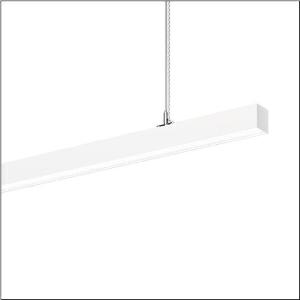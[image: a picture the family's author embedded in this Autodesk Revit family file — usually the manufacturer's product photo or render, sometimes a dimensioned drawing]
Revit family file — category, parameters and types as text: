
# Revit family: silica_r__21_51mx30tct9w_581c
name_source: partatom
category: Lighting Fixtures
units: mm (PartAtom-declared; Revit-internal decimal feet)

## family parameters
Cut with Voids When Loaded = No
Host = Face
Light Source = No
Part Type = Normal
Room Calculation Point = No
Round Connector Dimension = Use Diameter
Shared = No

## types (1)
- --- (1 x LED, 10300 lm, 84.4 W, 6500K)
    Apparent Load = 84 VA
    CIE Flux Codes = 47 79 96 58 100
    Color Rendering = 80
    Color Temperature = 6500K
    Default Elevation = 1800 mm
    Description = Silica® 21, office luminaire, primary optical cover: cover, of PMMA, opal, light emission: direct/indirect distribution, primary light characteristic: symmetric, installation type: suspended mounting, LED, rated luminous flux: 10.300lm, luminous efficacy: 116lm/W, light colour: 8tw, colour temperature: 2700..6500K, control gear: ECG DALI, with terminal, 3+2-pole, max. 2.5mm², mains connection: 220..240V, AC, 50/60Hz, rated input power: 88.7W, luminaire housing, of aluminium, traffic white (RAL 9016), length: 3.004mm, width: 53mm, height: 53mm, protection rating (complete): IP20, insulation class (complete): insulation class I (protective earthing), certification: CE, permissible operating ambient temperature: 0..+35°C, standard: EN 50419, packaging unit: 1 piece
    Height = 53 mm
    Lamp = 1 x LED
    Lamp Light Flux = 10300 lm
    Lamp Power = 84.4 W
    Lamp count = 1
    Length = 3004 mm
    Luminous efficacy = 122 lm/W
    Manufacturer = Siteco
    ModVariant = No
    Model = 51MX30TCT9W
    Mounting Place = Ceiling
    Mounting Type = Pendant
    Number of Poles = 1
    OnlyDefault = Yes
    Power Factor = 1
    Product Name = Silica® 21
    Product group = office luminaire | ceiling pendant
    ProductGroupID = 902
    Protection Class = Protection class I
    Protection Degree = IP 20
    RLX_Detail_Level = 1
    RLX_Emergency_Light_Flux = 0 lm
    RLX_Emergency_Type = 0
    RLX_Emergency_Type_DB = No
    RlxData = <blob elided: 18049 chars, md5=96d5f7a0>
    Socket = socket
    Standby Power = 0 W
    System Light Flux = 10300 lm
    System Power = 84 W
    Type Comments = individual setting
    Type Image = l_1313629.jpg
    URL = http://relux.com
    VarID = @adj_089013
    Voltage = 0 V
    Weight = 0.00 kg
    Width = 53 mm

## geometry (parser evidence)
native form markers: Blend x4, Sweep x16
no freeform markers — native parametric forms only
